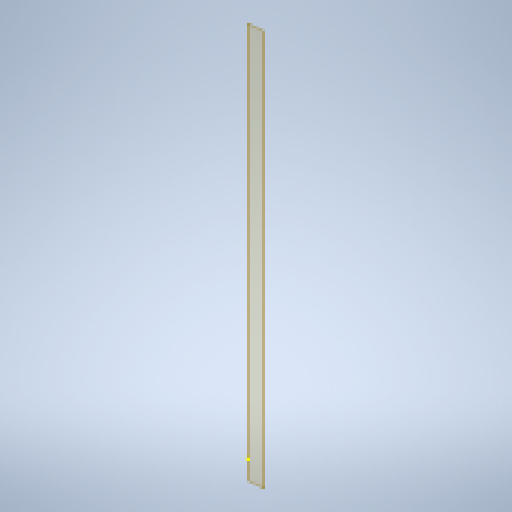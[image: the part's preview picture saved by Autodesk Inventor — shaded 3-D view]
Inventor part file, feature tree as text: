
AUTODESK INVENTOR PART (.ipt)
format: ipt  version: 2025 (Build 290162000, 162)  size: 139,264 bytes
history: native  units: in
note: dims shown in document units (in); Inventor stores cm internally (conversion verified against a paired STEP export)
features: plane x1, extrude x1, sketch x1
ambient origin geometry x8: Origin, YZ Plane, XZ Plane, XY Plane, X Axis, Y Axis, Z Axis, Center Point
bodies: Solid1 (feature_tree)
feature tree (3):
  plane  "Work Plane5"
  extrude  "Extrusion1"  Depth=4.0in
  sketch  "Sketch2"  dims[d0=4.0in d1=4.0in d2=55.0in d3=0.0in]
